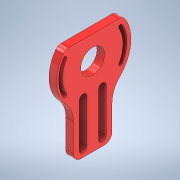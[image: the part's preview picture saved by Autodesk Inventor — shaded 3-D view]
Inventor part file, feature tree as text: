
AUTODESK INVENTOR PART (.ipt)
format: ipt  version: 2021 (Build 250183000, 183)  size: 182,784 bytes
history: native  units: in
note: dims shown in document units (in); Inventor stores cm internally (conversion verified against a paired STEP export)
features: sketch x2, extrude x1
ambient origin geometry x8: Origin, YZ Plane, XZ Plane, XY Plane, X Axis, Y Axis, Z Axis, Center Point
bodies: Solid1 (feature_tree)
feature tree (3):
  sketch  "Sketch1"  dims[d0=2.4803in d1=6.2992in]
  extrude  "Extrusion1"  Depth=6.2992in
  sketch  "Sketch2"  dims[d2=7.0866in d3=8.2677in d4=120.0deg d5=60.0deg d6=60.0deg d7=60.0deg d8=0.3937in d9=0.3937in d10=2.8543in d11=0.6102in d12=0.7874in d13=0.6102in d14=4.5472in d15=0.6102in d16=0.7874in d17=0.6102in d18=0.7874in d20=0.7874in d21=0.7874in d22=4.5472in d23=2.7559in d24=2.7559in d25=2.4606in d26=0.7874in d27=0.7874in d28=0.7874in d29=0.0in]
